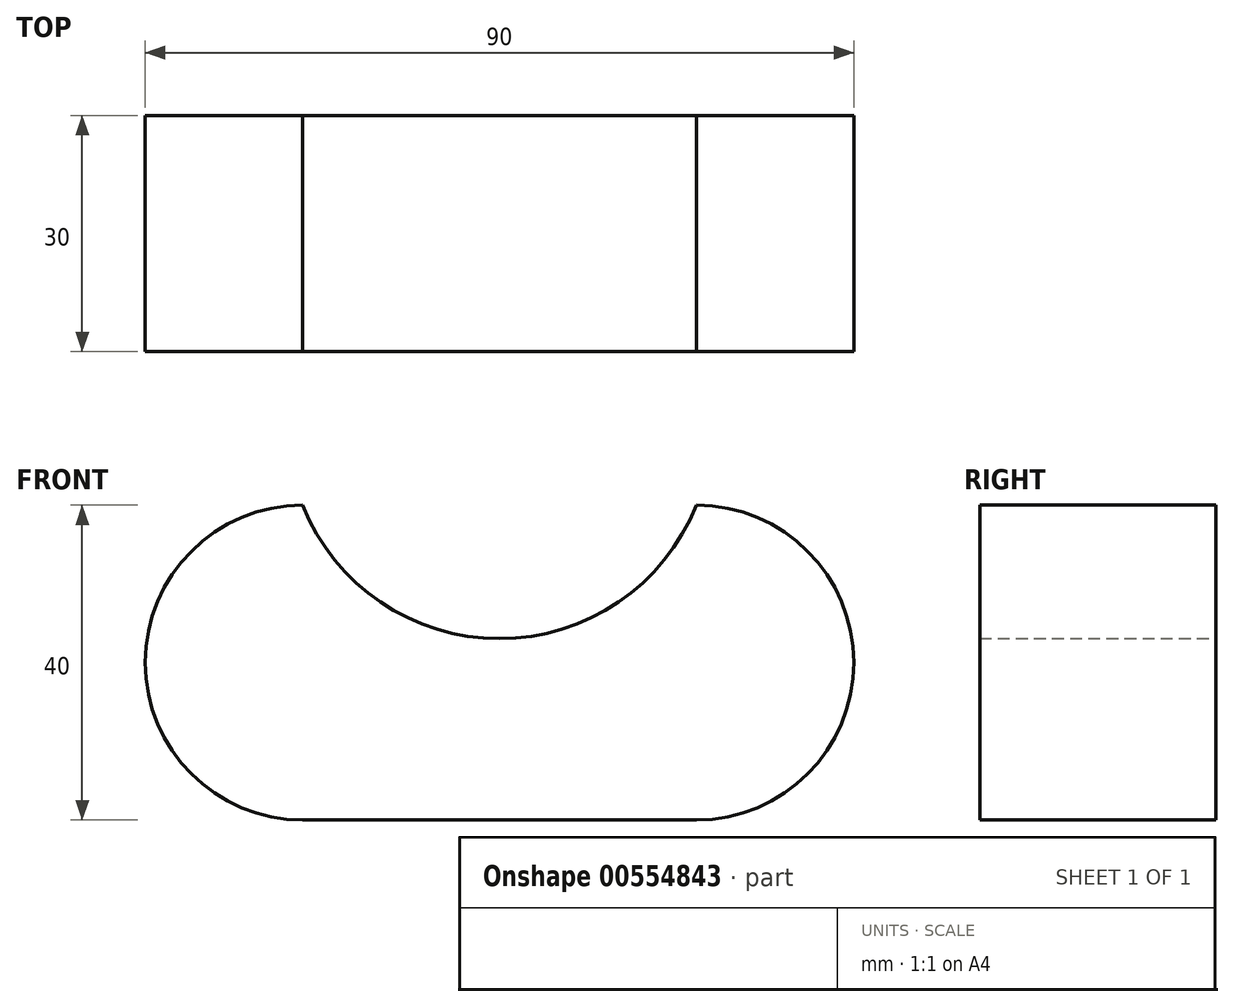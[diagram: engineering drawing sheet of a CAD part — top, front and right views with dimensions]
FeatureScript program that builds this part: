
annotation { "Feature Type Name" : "Feature", "Feature Type Description" : "" }
export const myFeature = defineFeature(function(context is Context, id is Id, definition is map)
    precondition{}
    {
        {
            var Q0;
            Q0=qCreatedBy(makeId("Front.planeOp"),FACE);
            var sketch = newSketch(context, id + "F0", { "sketchPlane" : qUnion([Q0])});
            skLineSegment(sketch, "E0", {"start": v(-29.55, -32.6) * mm, "end": v(20.45, -32.6) * mm});
            skArc(sketch, "E1", {"start": v(-29.55, 7.4) * mm, "mid": v(-49.55, -12.6) * mm, "end": v(-29.55, -32.6) * mm});
            skArc(sketch, "E2", {"start": v(20.45, -32.6) * mm, "mid": v(40.45, -12.6) * mm, "end": v(20.45, 7.4) * mm});
            skArc(sketch, "E3", {"start": v(-29.55, 7.4) * mm, "mid": v(-4.55, -9.55) * mm, "end": v(20.45, 7.4) * mm});
            skSolve(sketch);
        }
        {
            var Q0;
            Q0 = qSketchRegion(id + "F0", true);
            extrude(context, id + "F1", {"entities" : qUnion([Q0]), "depth" : 30 * mm, "offsetDistance" : 25 * mm});
        }
    });
